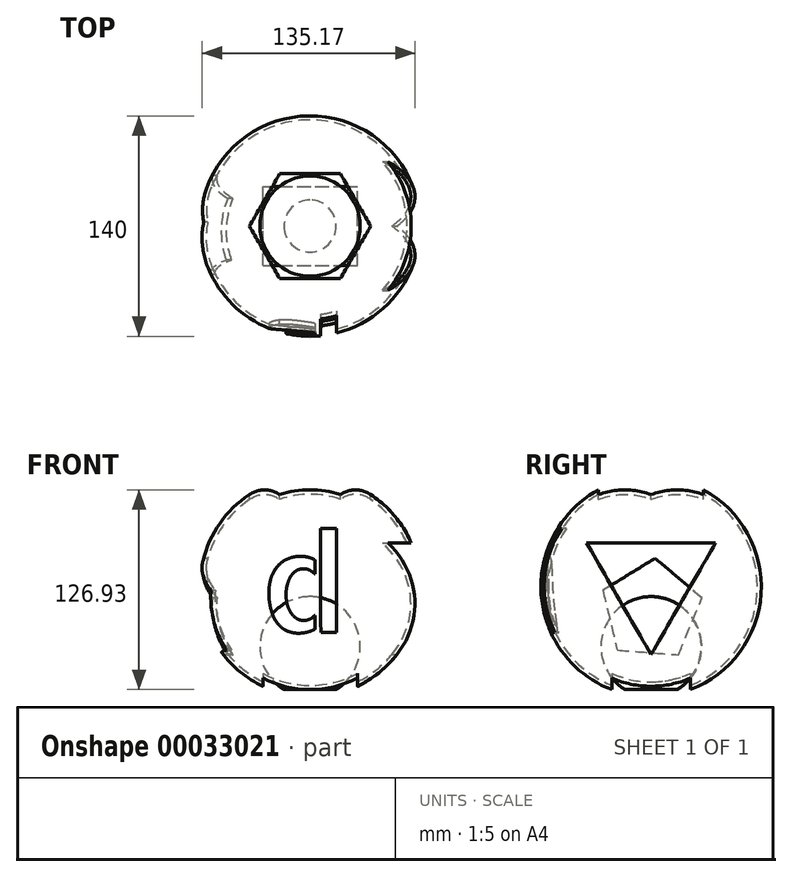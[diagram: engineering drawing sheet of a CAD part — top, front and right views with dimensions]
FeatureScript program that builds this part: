
annotation { "Feature Type Name" : "Feature", "Feature Type Description" : "" }
export const myFeature = defineFeature(function(context is Context, id is Id, definition is map)
    precondition{}
    {
        {
            var Q0;
            Q0=qCreatedBy(makeId("Front.planeOp"),FACE);
            var sketch = newSketch(context, id + "F0", { "sketchPlane" : qUnion([Q0])});
            skArc(sketch, "E0", {"start": v(0, 140) * mm, "mid": v(-70, 70) * mm, "end": v(0, 0) * mm});
            skLineSegment(sketch, "E1", {"start": v(0, 140) * mm, "end": v(0, 0) * mm});
            skSolve(sketch);
        }
        {
            var Q0;
            Q0 = qSketchRegion(id + "F0", true);
            var Q1;
            Q1=sQuery(id+"F0.wireOp",EDGE,"E1");
            revolve(context, id + "F1", {"entities" : qUnion([Q0]), "axis" : qUnion([Q1]), "revolveType" : RevolveType.FULL});
        }
        {
            var Q0;
            Q0=makeQuery(id+"F1.opRevolve","SWEPT_FACE",FACE,{"disambiguationData":[OSD([sQuery(id+"F0.wireOp",EDGE,"E0")])]});
            var Q1;
            Q1=makeQuery(id+"F1.opRevolve","SWEPT_BODY",BODY,{"disambiguationData":[OSD([sQuery(id+"F0.wireOp",EDGE,"E0"),sQuery(id+"F0.wireOp",EDGE,"E1")])]});
            shell(context, id + "F2", {"isHollow" : true, "entities" : qUnion([Q0]), "parts" : qUnion([Q1]), "thickness" : 2.5 * mm});
        }
        {
            var Q0;
            Q0=qCreatedBy(makeId("Top.planeOp"),FACE);
            var sketch = newSketch(context, id + "F3", { "sketchPlane" : qUnion([Q0])});
            skLineSegment(sketch, "E2.rect.bottom", {"start": v(30, 25) * mm, "end": v(-30, 25) * mm});
            skLineSegment(sketch, "E2.rect.top", {"start": v(30, -25) * mm, "end": v(-30, -25) * mm});
            skLineSegment(sketch, "E2.rect.left", {"start": v(30, 25) * mm, "end": v(30, -25) * mm});
            skLineSegment(sketch, "E2.rect.right", {"start": v(-30, 25) * mm, "end": v(-30, -25) * mm});
            skPoint(sketch, "E2.rect.middle", {"position": v(0, 0) * mm});
            skSolve(sketch);
        }
        {
            var Q0;
            Q0 = qSketchRegion(id + "F3", true);
            extrude(context, id + "F4", {"entities" : qUnion([Q0]), "operationType" : NewBodyOperationType.REMOVE, "depth" : 25 * mm});
        }
        {
            var Q0;
            Q0=qCreatedBy(makeId("Top.planeOp"),FACE);
            cPlane(context, id + "F5", {"entities" : qUnion([Q0]), "cplaneType" : CPlaneType.OFFSET, "offset" : 140 * mm, "width" : 150 * mm, "height" : 150 * mm});
        }
        {
            var Q0;
            Q0=qCreatedBy(id+"F5.planeOp",FACE);
            var sketch = newSketch(context, id + "F6", { "sketchPlane" : qUnion([Q0])});
            skCircle(sketch, "E3.cCircle", {"center": v(0, 0) * mm, "radius": 38.5 * mm, "construction": true});
            skLineSegment(sketch, "E3.0", {"start": v(-38.5, 0) * mm, "end": v(-19.25, 33.34) * mm});
            skLineSegment(sketch, "E3.1", {"start": v(-19.25, 33.34) * mm, "end": v(19.25, 33.34) * mm});
            skLineSegment(sketch, "E3.2", {"start": v(19.25, 33.34) * mm, "end": v(38.5, 0) * mm});
            skLineSegment(sketch, "E3.3", {"start": v(38.5, 0) * mm, "end": v(19.25, -33.34) * mm});
            skLineSegment(sketch, "E3.4", {"start": v(19.25, -33.34) * mm, "end": v(-19.25, -33.34) * mm});
            skLineSegment(sketch, "E3.5", {"start": v(-19.25, -33.34) * mm, "end": v(-38.5, 0) * mm});
            skSolve(sketch);
        }
        {
            var Q0;
            Q0 = qSketchRegion(id + "F6", true);
            extrude(context, id + "F7", {"entities" : qUnion([Q0]), "operationType" : NewBodyOperationType.REMOVE, "oppositeDirection" : true, "depth" : 25 * mm});
        }
        {
            var Q0;
            Q0=qCreatedBy(makeId("Right.planeOp"),FACE);
            cPlane(context, id + "F8", {"entities" : qUnion([Q0]), "cplaneType" : CPlaneType.OFFSET, "offset" : 70 * mm, "width" : 150 * mm, "height" : 150 * mm});
        }
        {
            var Q0;
            Q0=qCreatedBy(id+"F8.planeOp",FACE);
            var sketch = newSketch(context, id + "F9", { "sketchPlane" : qUnion([Q0])});
            skCircle(sketch, "E4.cCircle", {"center": v(0, 74.22) * mm, "radius": 47.3 * mm, "construction": true});
            skLineSegment(sketch, "E4.0", {"start": v(0, 26.93) * mm, "end": v(-40.96, 97.87) * mm});
            skLineSegment(sketch, "E4.1", {"start": v(-40.96, 97.87) * mm, "end": v(40.96, 97.87) * mm});
            skLineSegment(sketch, "E4.2", {"start": v(40.96, 97.87) * mm, "end": v(0, 26.93) * mm});
            skSolve(sketch);
        }
        {
            var Q0;
            Q0 = qSketchRegion(id + "F9", true);
            extrude(context, id + "F10", {"entities" : qUnion([Q0]), "operationType" : NewBodyOperationType.REMOVE, "oppositeDirection" : true, "depth" : 25 * mm});
        }
        {
            var Q0;
            Q0=qCreatedBy(makeId("Right.planeOp"),FACE);
            cPlane(context, id + "F11", {"entities" : qUnion([Q0]), "cplaneType" : CPlaneType.OFFSET, "offset" : 70 * mm, "oppositeDirection" : true, "width" : 150 * mm, "height" : 150 * mm});
        }
        {
            var Q0;
            Q0=qCreatedBy(id+"F11.planeOp",FACE);
            var sketch = newSketch(context, id + "F12", { "sketchPlane" : qUnion([Q0])});
            skCircle(sketch, "E5.cCircle", {"center": v(0, 55) * mm, "radius": 33.18 * mm, "construction": true});
            skLineSegment(sketch, "E5.0", {"start": v(17.36, 26.72) * mm, "end": v(-21.53, 29.75) * mm});
            skLineSegment(sketch, "E5.1", {"start": v(-21.53, 29.75) * mm, "end": v(-30.67, 67.67) * mm});
            skLineSegment(sketch, "E5.2", {"start": v(-30.67, 67.67) * mm, "end": v(2.57, 88.08) * mm});
            skLineSegment(sketch, "E5.3", {"start": v(2.57, 88.08) * mm, "end": v(32.26, 62.78) * mm});
            skLineSegment(sketch, "E5.4", {"start": v(32.26, 62.78) * mm, "end": v(17.36, 26.72) * mm});
            skSolve(sketch);
        }
        {
            var Q0;
            Q0 = qSketchRegion(id + "F12", true);
            extrude(context, id + "F13", {"entities" : qUnion([Q0]), "operationType" : NewBodyOperationType.REMOVE, "depth" : 25 * mm});
        }
        {
            var Q0;
            Q0=qCreatedBy(makeId("Front.planeOp"),FACE);
            cPlane(context, id + "F14", {"entities" : qUnion([Q0]), "cplaneType" : CPlaneType.OFFSET, "offset" : 70 * mm, "width" : 150 * mm, "height" : 150 * mm});
        }
        {
            var Q0;
            Q0=qCreatedBy(id+"F14.planeOp",FACE);
            var sketch = newSketch(context, id + "F15", { "sketchPlane" : qUnion([Q0])});
            skText(sketch, "E6", { "text": "d", "fontName": "AllertaStencil-Regular.ttf"});
            const initialGuessF15  = {"E6": [-0.03044, 0.04086, 1, 0, 0.06281]};
            skSetInitialGuess(sketch, initialGuessF15);
            skSolve(sketch);
        }
        {
            var Q0;
            Q0 = qSketchRegion(id + "F15", true);
            extrude(context, id + "F16", {"entities" : qUnion([Q0]), "operationType" : NewBodyOperationType.REMOVE, "oppositeDirection" : true, "depth" : 25 * mm});
        }
        {
            var Q0;
            Q0=qCreatedBy(makeId("Right.planeOp"),FACE);
            var sketch = newSketch(context, id + "F17", { "sketchPlane" : qUnion([Q0])});
            skLineSegment(sketch, "E7.0", {"start": v(25, 11.9) * mm, "end": v(25, 4.62) * mm});
            skLineSegment(sketch, "E8.0", {"start": v(-25, 11.9) * mm, "end": v(-25, 4.62) * mm});
            skLineSegment(sketch, "E9", {"start": v(25, 4.62) * mm, "end": v(-25, 4.62) * mm});
            skLineSegment(sketch, "E10", {"start": v(25, 4.62) * mm, "end": v(25, 0) * mm});
            skSolve(sketch);
        }
        {
            var Q0;
            Q0=qCreatedBy(makeId("Right.planeOp"),FACE);
            var sketch = newSketch(context, id + "F18", { "sketchPlane" : qUnion([Q0])});
            skLineSegment(sketch, "E11.0", {"start": v(0, 4.62) * mm, "end": v(-16.52, 4.62) * mm});
            skArc(sketch, "E12", {"start": v(0, 63.7) * mm, "mid": v(-30.68, 40.43) * mm, "end": v(-16.52, 4.62) * mm});
            skPoint(sketch, "E12.centerSnap0", {"position": v(0, 4.62) * mm});
            skLineSegment(sketch, "E13", {"start": v(0, 4.62) * mm, "end": v(0, 63.7) * mm});
            skSolve(sketch);
        }
        {
            var Q0;
            Q0 = qSketchRegion(id + "F18", true);
            var Q1;
            Q1=sQuery(id+"F18.wireOp",EDGE,"E13");
            revolve(context, id + "F19", {"entities" : qUnion([Q0]), "axis" : qUnion([Q1]), "revolveType" : RevolveType.FULL});
        }
    });
